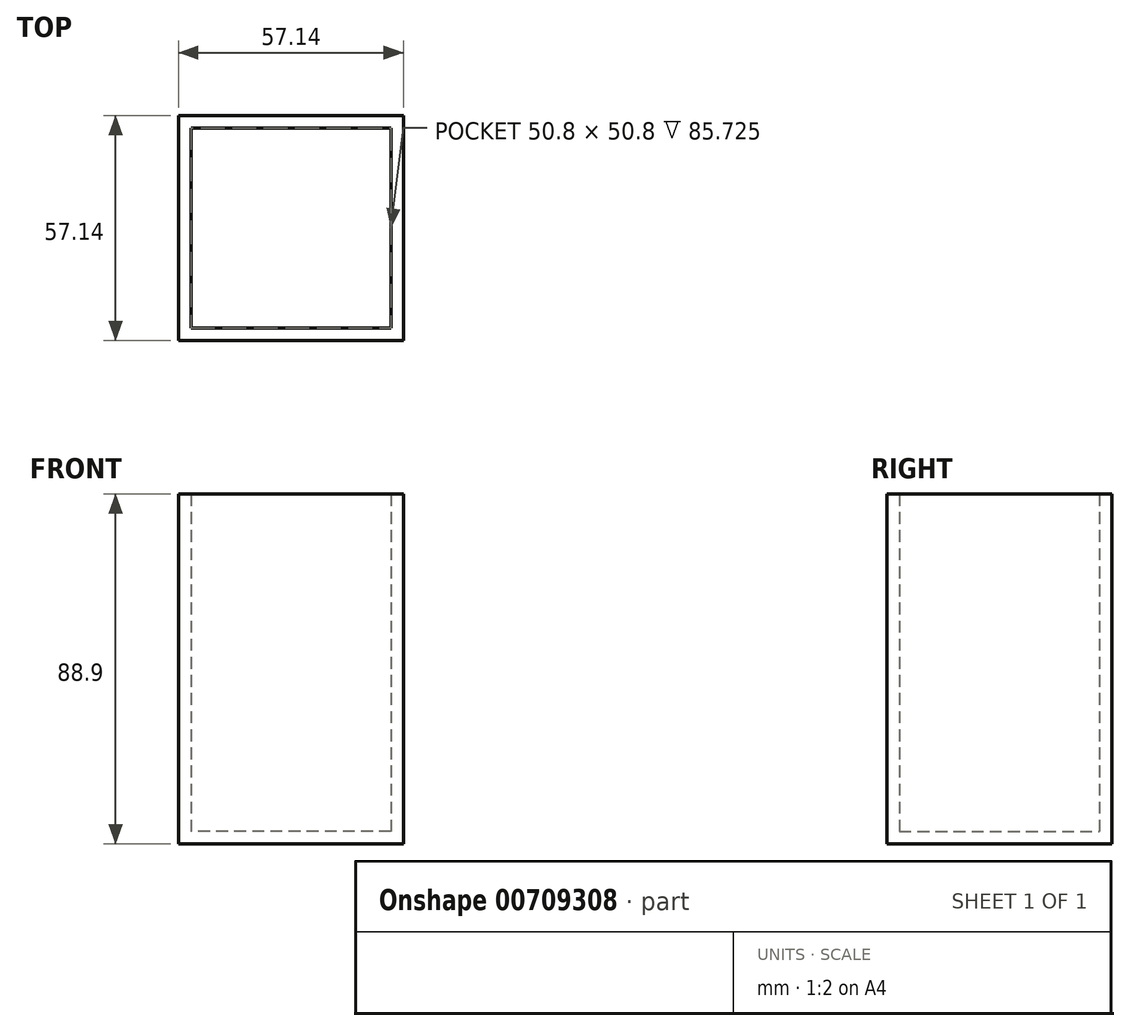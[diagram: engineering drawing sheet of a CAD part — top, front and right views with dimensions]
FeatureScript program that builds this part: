
annotation { "Feature Type Name" : "Feature", "Feature Type Description" : "" }
export const myFeature = defineFeature(function(context is Context, id is Id, definition is map)
    precondition{}
    {
        {
            var Q0;
            Q0=qCreatedBy(makeId("Top.planeOp"),FACE);
            var sketch = newSketch(context, id + "F0", { "sketchPlane" : qUnion([Q0])});
            skLineSegment(sketch, "E0.bottom", {"start": v(25.4, -25.4) * mm, "end": v(-25.4, -25.4) * mm});
            skLineSegment(sketch, "E0.top", {"start": v(25.4, 25.4) * mm, "end": v(-25.4, 25.4) * mm});
            skLineSegment(sketch, "E0.left", {"start": v(25.4, -25.4) * mm, "end": v(25.4, 25.4) * mm});
            skLineSegment(sketch, "E0.right", {"start": v(-25.4, -25.4) * mm, "end": v(-25.4, 25.4) * mm});
            skPoint(sketch, "E0.middle", {"position": v(0, 0) * mm});
            skSolve(sketch);
        }
        {
            var Q0;
            Q0 = qSketchRegion(id + "F0", true);
            extrude(context, id + "F1", {"entities" : qUnion([Q0]), "depth" : 3.17 * mm, "offsetDistance" : 25.4 * mm});
        }
        {
            var Q0;
            Q0=makeQuery(id+"F1.opExtrude","SWEPT_FACE",FACE,{"disambiguationData":[OSD([sQuery(id+"F0.wireOp",EDGE,"E0.bottom")])]});
            var sketch = newSketch(context, id + "F2", { "sketchPlane" : qUnion([Q0])});
            skLineSegment(sketch, "E1.bottom", {"start": v(-28.57, 0) * mm, "end": v(28.58, 0) * mm});
            skLineSegment(sketch, "E1.top", {"start": v(-28.58, 88.9) * mm, "end": v(28.58, 88.9) * mm});
            skLineSegment(sketch, "E1.left", {"start": v(-28.57, 0) * mm, "end": v(-28.58, 88.9) * mm});
            skLineSegment(sketch, "E1.right", {"start": v(28.58, 0) * mm, "end": v(28.58, 88.9) * mm});
            skSolve(sketch);
        }
        {
            var Q0;
            Q0 = qSketchRegion(id + "F2", true);
            extrude(context, id + "F3", {"entities" : qUnion([Q0]), "operationType" : NewBodyOperationType.ADD, "depth" : 3.17 * mm, "offsetDistance" : 25.4 * mm});
        }
        {
            var Q0;
            Q0=makeQuery(id+"F1.opExtrude","SWEPT_FACE",FACE,{"disambiguationData":[OSD([sQuery(id+"F0.wireOp",EDGE,"E0.top")])]});
            var sketch = newSketch(context, id + "F4", { "sketchPlane" : qUnion([Q0])});
            skLineSegment(sketch, "E2.bottom", {"start": v(-28.58, 0) * mm, "end": v(28.58, 0) * mm});
            skLineSegment(sketch, "E2.top", {"start": v(-28.58, 88.9) * mm, "end": v(28.57, 88.9) * mm});
            skLineSegment(sketch, "E2.left", {"start": v(-28.58, 0) * mm, "end": v(-28.58, 88.9) * mm});
            skLineSegment(sketch, "E2.right", {"start": v(28.58, 0) * mm, "end": v(28.57, 88.9) * mm});
            skSolve(sketch);
        }
        {
            var Q0;
            Q0 = qSketchRegion(id + "F4", true);
            extrude(context, id + "F5", {"entities" : qUnion([Q0]), "operationType" : NewBodyOperationType.ADD, "depth" : 3.17 * mm, "offsetDistance" : 25.4 * mm});
        }
        {
            var Q0;
            Q0=makeQuery(id+"F1.opExtrude","SWEPT_FACE",FACE,{"disambiguationData":[OSD([sQuery(id+"F0.wireOp",EDGE,"E0.left")])]});
            var sketch = newSketch(context, id + "F6", { "sketchPlane" : qUnion([Q0])});
            skLineSegment(sketch, "E3.bottom", {"start": v(-25.4, 0) * mm, "end": v(25.4, 0) * mm});
            skLineSegment(sketch, "E3.top", {"start": v(-25.4, 88.9) * mm, "end": v(25.4, 88.9) * mm});
            skLineSegment(sketch, "E3.left", {"start": v(-25.4, 0) * mm, "end": v(-25.4, 88.9) * mm});
            skLineSegment(sketch, "E3.right", {"start": v(25.4, 0) * mm, "end": v(25.4, 88.9) * mm});
            skSolve(sketch);
        }
        {
            var Q0;
            Q0 = qSketchRegion(id + "F6", true);
            extrude(context, id + "F7", {"entities" : qUnion([Q0]), "operationType" : NewBodyOperationType.ADD, "depth" : 3.17 * mm, "offsetDistance" : 25.4 * mm});
        }
        {
            var Q0;
            Q0=makeQuery(id+"F1.opExtrude","SWEPT_FACE",FACE,{"disambiguationData":[OSD([sQuery(id+"F0.wireOp",EDGE,"E0.right")])]});
            var sketch = newSketch(context, id + "F8", { "sketchPlane" : qUnion([Q0])});
            skLineSegment(sketch, "E4.bottom", {"start": v(-25.4, 0) * mm, "end": v(25.4, 0) * mm});
            skLineSegment(sketch, "E4.top", {"start": v(-25.4, 88.9) * mm, "end": v(25.4, 88.9) * mm});
            skLineSegment(sketch, "E4.left", {"start": v(-25.4, 0) * mm, "end": v(-25.4, 88.9) * mm});
            skLineSegment(sketch, "E4.right", {"start": v(25.4, 0) * mm, "end": v(25.4, 88.9) * mm});
            skSolve(sketch);
        }
        {
            var Q0;
            Q0 = qSketchRegion(id + "F8", true);
            extrude(context, id + "F9", {"entities" : qUnion([Q0]), "operationType" : NewBodyOperationType.ADD, "depth" : 3.17 * mm, "offsetDistance" : 25.4 * mm});
        }
    });
